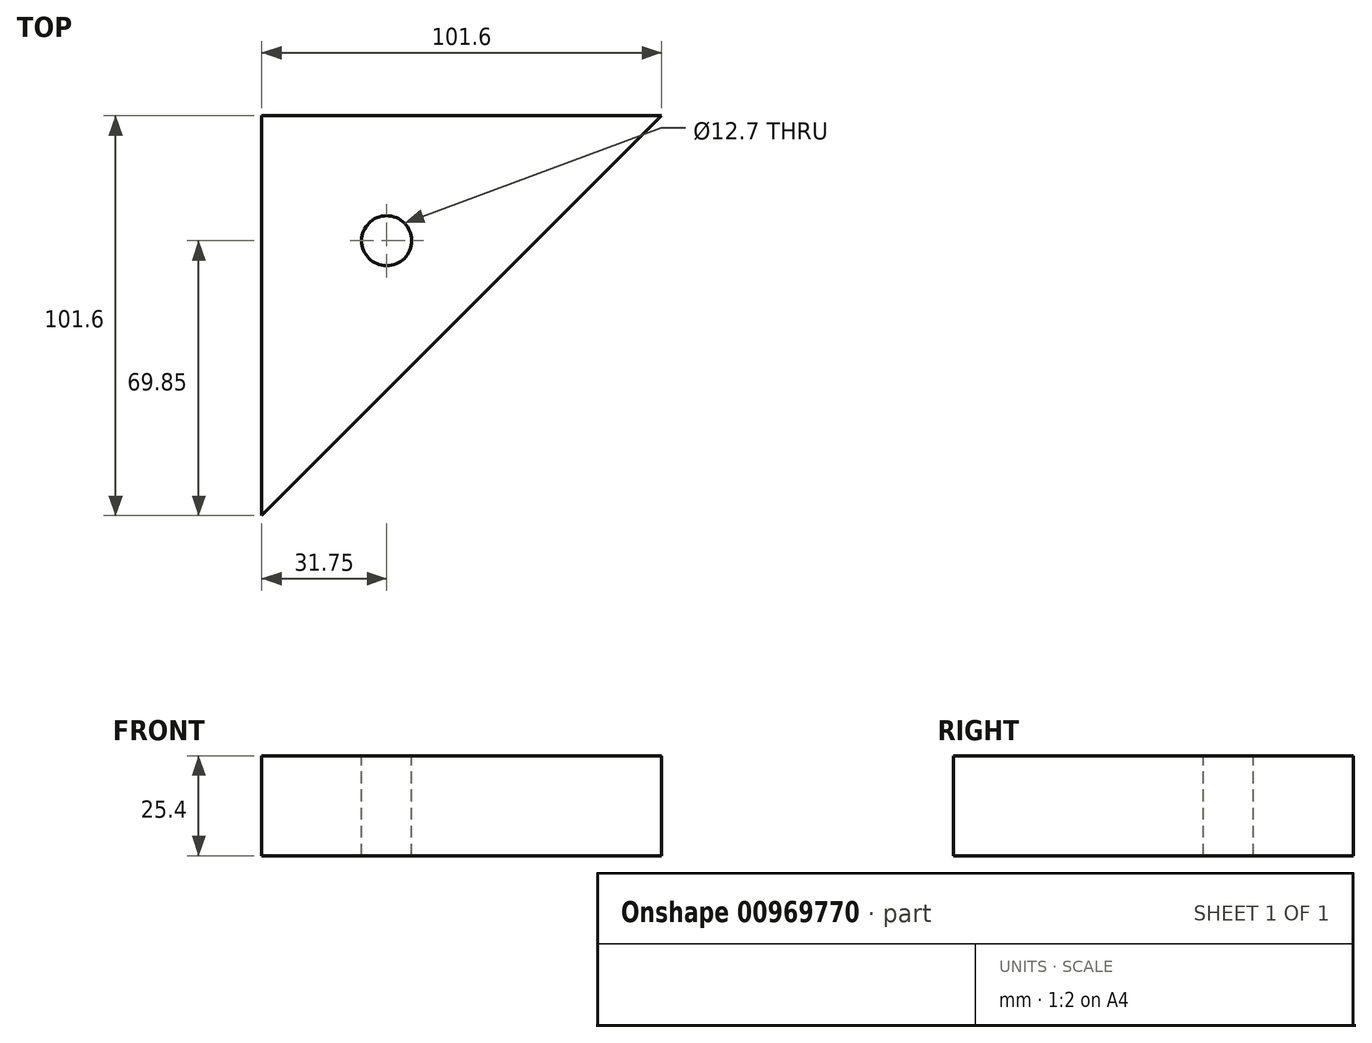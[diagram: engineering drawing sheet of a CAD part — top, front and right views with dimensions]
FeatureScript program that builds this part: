
annotation { "Feature Type Name" : "Feature", "Feature Type Description" : "" }
export const myFeature = defineFeature(function(context is Context, id is Id, definition is map)
    precondition{}
    {
        {
            var Q0;
            Q0=qCreatedBy(makeId("Top.planeOp"),FACE);
            var sketch = newSketch(context, id + "F0", { "sketchPlane" : qUnion([Q0])});
            skLineSegment(sketch, "E0", {"start": v(0, 0) * mm, "end": v(0, 101.6) * mm});
            skLineSegment(sketch, "E1", {"start": v(0, 101.6) * mm, "end": v(101.6, 101.6) * mm});
            skLineSegment(sketch, "E2", {"start": v(101.6, 101.6) * mm, "end": v(0, 0) * mm});
            skSolve(sketch);
        }
        {
            var Q0;
            Q0 = qSketchRegion(id + "F0", true);
            extrude(context, id + "F1", {"entities" : qUnion([Q0]), "depth" : 25.4 * mm, "offsetDistance" : 25.4 * mm});
        }
        {
            var Q0;
            Q0=makeQuery(id+"F1.opExtrude","CAP_FACE",FACE,{"disambiguationData":[OSD([sQuery(id+"F0.wireOp",EDGE,"E0"),sQuery(id+"F0.wireOp",EDGE,"E1"),sQuery(id+"F0.wireOp",EDGE,"E2")])],"isStart":false});
            var sketch = newSketch(context, id + "F2", { "sketchPlane" : qUnion([Q0])});
            skPoint(sketch, "E3", {"position": v(31.75, 69.85) * mm});
            skCircle(sketch, "E4", {"center": v(31.75, 69.85) * mm, "radius": 6.35 * mm});
            skSolve(sketch);
        }
        {
            var Q0;
            Q0 = qSketchRegion(id + "F2", true);
            extrude(context, id + "F3", {"entities" : qUnion([Q0]), "operationType" : NewBodyOperationType.REMOVE, "oppositeDirection" : true, "depth" : 25.4 * mm, "offsetDistance" : 25.4 * mm});
        }
    });
